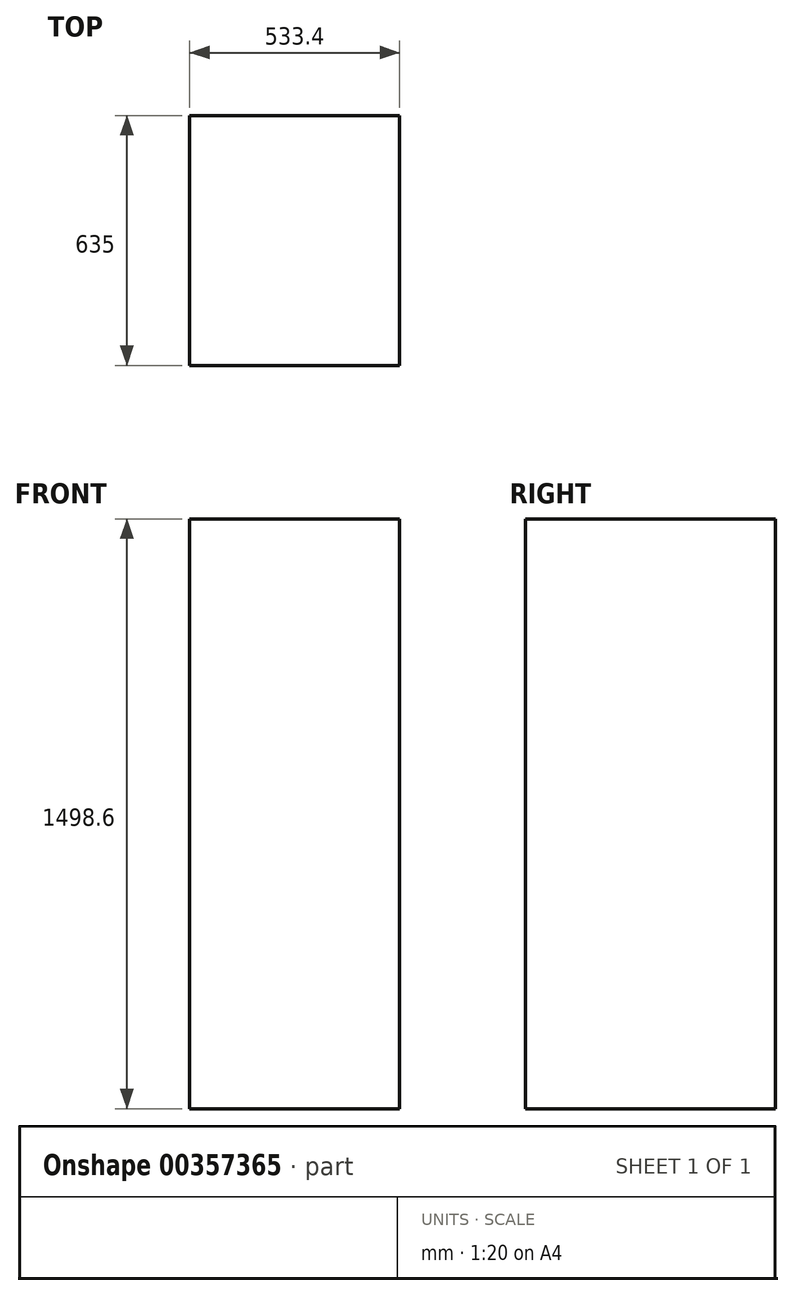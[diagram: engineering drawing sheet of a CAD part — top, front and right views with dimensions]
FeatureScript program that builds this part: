
annotation { "Feature Type Name" : "Feature", "Feature Type Description" : "" }
export const myFeature = defineFeature(function(context is Context, id is Id, definition is map)
    precondition{}
    {
        {
            var Q0;
            Q0=qCreatedBy(makeId("Top.planeOp"),FACE);
            var sketch = newSketch(context, id + "F0", { "sketchPlane" : qUnion([Q0])});
            skLineSegment(sketch, "E0.bottom", {"start": v(-266.7, -317.5) * mm, "end": v(266.7, -317.5) * mm});
            skLineSegment(sketch, "E0.top", {"start": v(-266.7, 317.5) * mm, "end": v(266.7, 317.5) * mm});
            skLineSegment(sketch, "E0.left", {"start": v(-266.7, -317.5) * mm, "end": v(-266.7, 317.5) * mm});
            skLineSegment(sketch, "E0.right", {"start": v(266.7, -317.5) * mm, "end": v(266.7, 317.5) * mm});
            skPoint(sketch, "E0.middle", {"position": v(0, 0) * mm});
            skSolve(sketch);
        }
        {
            var Q0;
            Q0 = qSketchRegion(id + "F0", true);
            extrude(context, id + "F1", {"entities" : qUnion([Q0]), "depth" : 1498.6 * mm});
        }
    });
